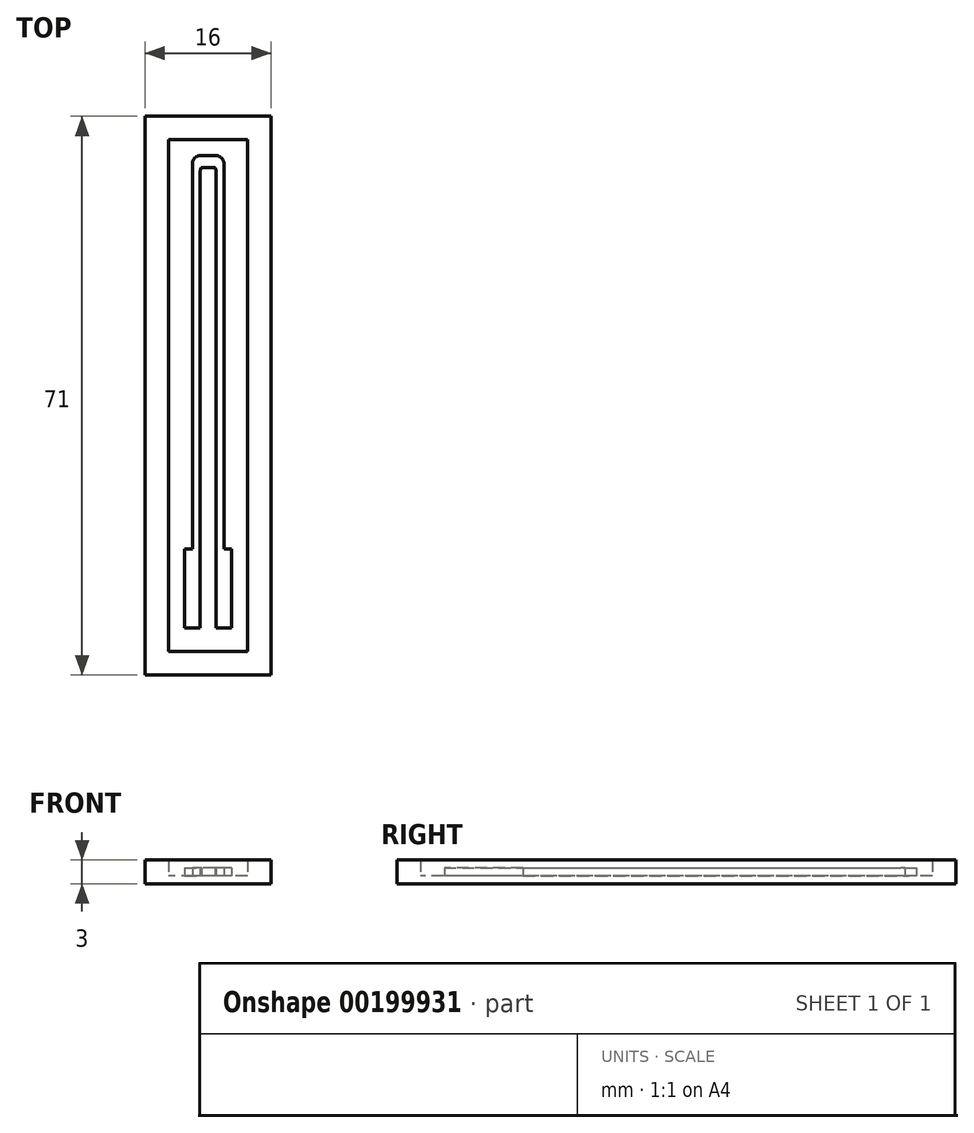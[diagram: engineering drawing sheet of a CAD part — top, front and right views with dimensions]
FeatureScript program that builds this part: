
annotation { "Feature Type Name" : "Feature", "Feature Type Description" : "" }
export const myFeature = defineFeature(function(context is Context, id is Id, definition is map)
    precondition{}
    {
        {
            var Q0;
            Q0=qCreatedBy(makeId("Top.planeOp"),FACE);
            var sketch = newSketch(context, id + "F0", { "sketchPlane" : qUnion([Q0])});
            skLineSegment(sketch, "E0.rect.bottom", {"start": v(5, 32.5) * mm, "end": v(-5, 32.5) * mm});
            skLineSegment(sketch, "E0.rect.top", {"start": v(5, -32.5) * mm, "end": v(-5, -32.5) * mm});
            skLineSegment(sketch, "E0.rect.left", {"start": v(5, 32.5) * mm, "end": v(5, -32.5) * mm});
            skLineSegment(sketch, "E0.rect.right", {"start": v(-5, 32.5) * mm, "end": v(-5, -32.5) * mm});
            skPoint(sketch, "E0.rect.middle", {"position": v(0, 0) * mm});
            skLineSegment(sketch, "E1", {"start": v(0, 0) * mm, "end": v(0, 17.9) * mm, "construction": true});
            skLineSegment(sketch, "E2.bottom", {"start": v(-3, -19.5) * mm, "end": v(-2, -19.5) * mm});
            skLineSegment(sketch, "E2.top", {"start": v(-3, -29.5) * mm, "end": v(-1, -29.5) * mm});
            skLineSegment(sketch, "E2.left", {"start": v(-3, -19.5) * mm, "end": v(-3, -29.5) * mm});
            skLineSegment(sketch, "E2.right", {"start": v(-1, -19.5) * mm, "end": v(-1, -29.5) * mm});
            skLineSegment(sketch, "E3", {"start": v(-1, -19.5) * mm, "end": v(-1, 28.5) * mm});
            skLineSegment(sketch, "E4", {"start": v(0, 29.5) * mm, "end": v(0, 29.5) * mm});
            skLineSegment(sketch, "E5", {"start": v(-2, -19.5) * mm, "end": v(-2, 29.5) * mm});
            skLineSegment(sketch, "E6", {"start": v(-1, 30.5) * mm, "end": v(0, 30.5) * mm});
            skPoint(sketch, "E7.visualSharp", {"position": v(-2, 30.5) * mm});
            skArc(sketch, "E7.filletArc", {"start": v(-1, 30.5) * mm, "mid": v(-1.7, 30.2) * mm, "end": v(-2, 29.5) * mm});
            skArc(sketch, "E8.filletArc", {"start": v(0, 29.5) * mm, "mid": v(-0.7, 29.2) * mm, "end": v(-1, 28.5) * mm});
            skLineSegment(sketch, "E9.0.MirrorCS", {"start": v(3, -29.5) * mm, "end": v(1, -29.5) * mm});
            skArc(sketch, "E9.1.MirrorCS", {"start": v(0, 29.5) * mm, "mid": v(0.7, 29.2) * mm, "end": v(1, 28.5) * mm});
            skArc(sketch, "E9.2.MirrorCS", {"start": v(1, 30.5) * mm, "mid": v(1.7, 30.2) * mm, "end": v(2, 29.5) * mm});
            skLineSegment(sketch, "E9.3.MirrorCS", {"start": v(3, -19.5) * mm, "end": v(2, -19.5) * mm});
            skLineSegment(sketch, "E9.5.MirrorCS", {"start": v(1, 30.5) * mm, "end": v(0, 30.5) * mm});
            skPoint(sketch, "E9.6.MirrorP", {"position": v(2, 30.5) * mm});
            skLineSegment(sketch, "E9.8.MirrorCS", {"start": v(1, -19.5) * mm, "end": v(1, -29.5) * mm});
            skPoint(sketch, "E9.9.MirrorP", {"position": v(1, 29.5) * mm});
            skLineSegment(sketch, "E9.10.MirrorCS", {"start": v(2, -19.5) * mm, "end": v(2, 29.5) * mm});
            skLineSegment(sketch, "E9.11.MirrorCS", {"start": v(3, -19.5) * mm, "end": v(3, -29.5) * mm});
            skLineSegment(sketch, "E9.12.MirrorCS", {"start": v(1, -19.5) * mm, "end": v(1, 28.5) * mm});
            skLineSegment(sketch, "E10.0", {"start": v(8, 35.5) * mm, "end": v(-8, 35.5) * mm});
            skLineSegment(sketch, "E10.1", {"start": v(8, 35.5) * mm, "end": v(8, -35.5) * mm});
            skLineSegment(sketch, "E10.2", {"start": v(8, -35.5) * mm, "end": v(-8, -35.5) * mm});
            skLineSegment(sketch, "E10.3", {"start": v(-8, 35.5) * mm, "end": v(-8, -35.5) * mm});
            skSolve(sketch);
        }
        {
            var Q0;
            Q0=makeQuery(id+"F0.imprint","IMPRINT",FACE,{"disambiguationData":[TD([[makeQuery(id+"F0.imprint","IMPRINT",EDGE,{"derivedFrom":sQuery(id+"F0.wireOp",EDGE,"E0.rect.bottom")}),-1.0]])]});
            extrude(context, id + "F1", {"entities" : qUnion([Q0]), "depth" : 2 * mm});
        }
        {
            var Q0;
            Q0=makeQuery(id+"F0.imprint","IMPRINT",FACE,{"disambiguationData":[TD([[makeQuery(id+"F0.imprint","IMPRINT",EDGE,{"derivedFrom":sQuery(id+"F0.wireOp",EDGE,"E0.rect.bottom")}),1.0]])]});
            var Q1;
            Q1=makeQuery(id+"F1.opExtrude","CAP_FACE",FACE,{"disambiguationData":[OSD([sQuery(id+"F0.wireOp",EDGE,"E0.rect.bottom"),sQuery(id+"F0.wireOp",EDGE,"E0.rect.top"),sQuery(id+"F0.wireOp",EDGE,"E0.rect.left"),sQuery(id+"F0.wireOp",EDGE,"E0.rect.right"),sQuery(id+"F0.wireOp",EDGE,"E10.0"),sQuery(id+"F0.wireOp",EDGE,"E10.1"),sQuery(id+"F0.wireOp",EDGE,"E10.2"),sQuery(id+"F0.wireOp",EDGE,"E10.3")])],"isStart":false});
            var Q2;
            Q2=makeQuery(id+"F0.imprint","IMPRINT",FACE,{"disambiguationData":[TD([[makeQuery(id+"F0.imprint","IMPRINT",EDGE,{"derivedFrom":sQuery(id+"F0.wireOp",EDGE,"E2.bottom")}),-1.0]])]});
            extrude(context, id + "F2", {"entities" : qUnion([Q0, Q1, Q2]), "operationType" : NewBodyOperationType.ADD, "depth" : 1 * mm});
        }
        {
            var Q0;
            Q0=makeQuery(id+"F2.opExtrude","CAP_FACE",FACE,{"disambiguationData":[OSD([sQuery(id+"F0.wireOp",EDGE,"E0.rect.bottom"),sQuery(id+"F0.wireOp",EDGE,"E0.rect.top"),sQuery(id+"F0.wireOp",EDGE,"E0.rect.left"),sQuery(id+"F0.wireOp",EDGE,"E0.rect.right")])],"isStart":false});
            var sketch = newSketch(context, id + "F3", { "sketchPlane" : qUnion([Q0])});
            skLineSegment(sketch, "E11.0", {"start": v(-3, -19.5) * mm, "end": v(-3, -29.5) * mm});
            skLineSegment(sketch, "E12.0", {"start": v(-3, -29.5) * mm, "end": v(-1, -29.5) * mm});
            skLineSegment(sketch, "E13.0", {"start": v(-1, -19.5) * mm, "end": v(-1, -29.5) * mm});
            skLineSegment(sketch, "E14.0", {"start": v(-3, -19.5) * mm, "end": v(-2, -19.5) * mm});
            skLineSegment(sketch, "E15.0", {"start": v(-2, -19.5) * mm, "end": v(-2, 29.5) * mm});
            skLineSegment(sketch, "E16.0", {"start": v(-1, -19.5) * mm, "end": v(-1, 28.5) * mm});
            skArc(sketch, "E17.0", {"start": v(-1, 30.5) * mm, "mid": v(-1.7, 30.2) * mm, "end": v(-2, 29.5) * mm});
            skArc(sketch, "E18.0", {"start": v(0, 29.5) * mm, "mid": v(-0.7, 29.2) * mm, "end": v(-1, 28.5) * mm});
            skLineSegment(sketch, "E19.0", {"start": v(-4, 29) * mm, "end": v(0, 29) * mm});
            skLineSegment(sketch, "E20.0", {"start": v(-1, 30.5) * mm, "end": v(0, 30.5) * mm});
            skLineSegment(sketch, "E21.0", {"start": v(4, 29) * mm, "end": v(0, 29) * mm});
            skLineSegment(sketch, "E22.0", {"start": v(1, 30.5) * mm, "end": v(0, 30.5) * mm});
            skArc(sketch, "E23.0", {"start": v(0, 29.5) * mm, "mid": v(0.7, 29.2) * mm, "end": v(1, 28.5) * mm});
            skArc(sketch, "E24.0", {"start": v(1, 30.5) * mm, "mid": v(1.7, 30.2) * mm, "end": v(2, 29.5) * mm});
            skLineSegment(sketch, "E25.0", {"start": v(1, -19.5) * mm, "end": v(1, 28.5) * mm});
            skLineSegment(sketch, "E26.0", {"start": v(2, -19.5) * mm, "end": v(2, 29.5) * mm});
            skLineSegment(sketch, "E27.0", {"start": v(1, -19.5) * mm, "end": v(1, -29.5) * mm});
            skLineSegment(sketch, "E28.0", {"start": v(3, -29.5) * mm, "end": v(1, -29.5) * mm});
            skLineSegment(sketch, "E29.0", {"start": v(3, -19.5) * mm, "end": v(3, -29.5) * mm});
            skLineSegment(sketch, "E30.0", {"start": v(3, -19.5) * mm, "end": v(2, -19.5) * mm});
            skSolve(sketch);
        }
        {
            var Q0;
            Q0=qSketchRegion(id+"F3",true);
            extrude(context, id + "F4", {"entities" : qUnion([Q0]), "operationType" : NewBodyOperationType.ADD, "depth" : 1 * mm});
        }
    });
